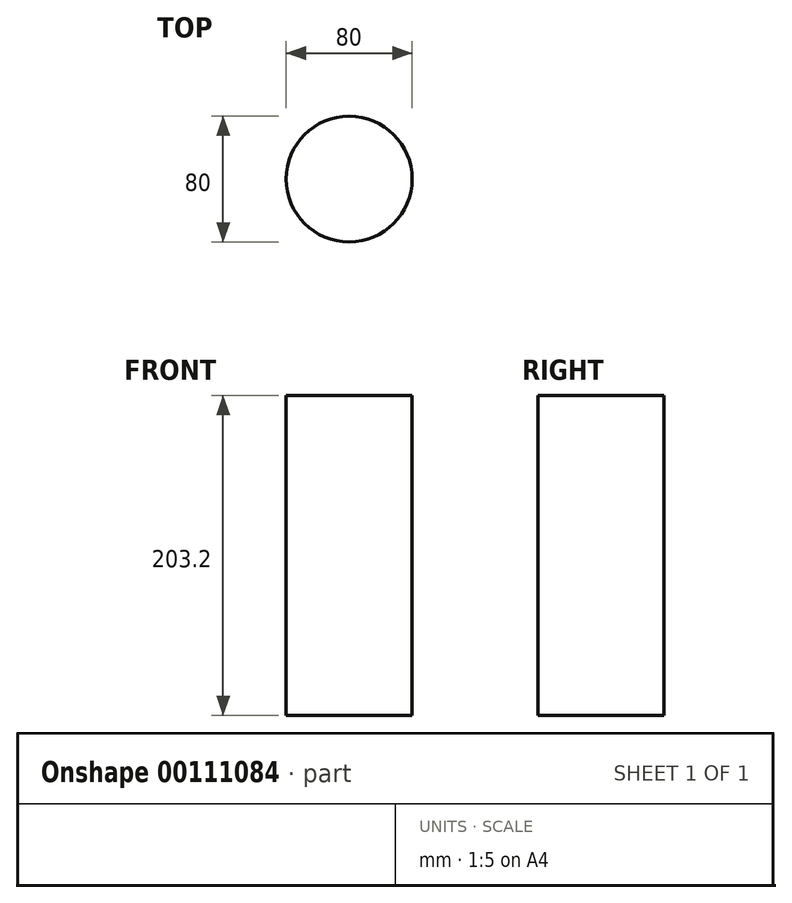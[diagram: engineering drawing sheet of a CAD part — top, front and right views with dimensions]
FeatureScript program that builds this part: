
annotation { "Feature Type Name" : "Feature", "Feature Type Description" : "" }
export const myFeature = defineFeature(function(context is Context, id is Id, definition is map)
    precondition{}
    {
        {
            var Q0;
            Q0=qCreatedBy(makeId("Top.planeOp"),FACE);
            var sketch = newSketch(context, id + "F0", { "sketchPlane" : qUnion([Q0])});
            skCircle(sketch, "E0", {"center": v(0, 0) * mm, "radius": 40 * mm});
            skSolve(sketch);
        }
        {
            var Q0;
            Q0=makeQuery(id+"F0.imprint","IMPRINT",FACE,{"disambiguationData":[TD([[makeQuery(id+"F0.imprint","IMPRINT",EDGE,{"derivedFrom":sQuery(id+"F0.wireOp",EDGE,"E0")}),1.0]])]});
            extrude(context, id + "F1", {"entities" : qUnion([Q0]), "oppositeDirection" : true, "depth" : 127 * mm});
        }
        {
            var Q0;
            Q0=makeQuery(id+"F0.imprint","IMPRINT",FACE,{"disambiguationData":[TD([[makeQuery(id+"F0.imprint","IMPRINT",EDGE,{"derivedFrom":sQuery(id+"F0.wireOp",EDGE,"E0")}),-1.0]])]});
            var Q1;
            Q1=makeQuery(id+"F0.imprint","IMPRINT",FACE,{"disambiguationData":[TD([[makeQuery(id+"F0.imprint","IMPRINT",EDGE,{"derivedFrom":sQuery(id+"F0.wireOp",EDGE,"E0")}),1.0]])]});
            extrude(context, id + "F2", {"entities" : qUnion([Q0, Q1]), "operationType" : NewBodyOperationType.ADD, "depth" : 76.2 * mm});
        }
    });
